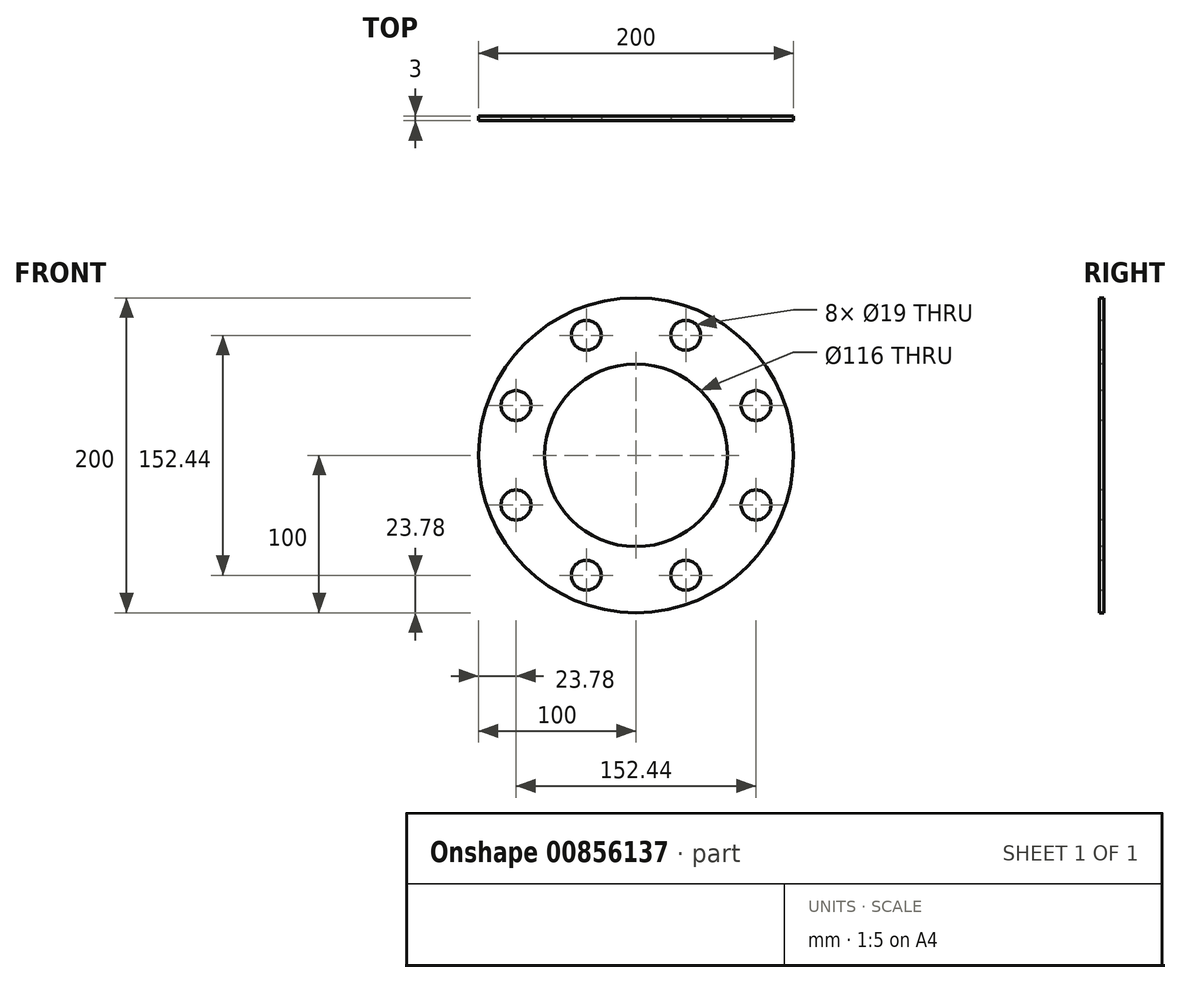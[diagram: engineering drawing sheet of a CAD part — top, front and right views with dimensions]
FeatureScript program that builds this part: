
annotation { "Feature Type Name" : "Feature", "Feature Type Description" : "" }
export const myFeature = defineFeature(function(context is Context, id is Id, definition is map)
    precondition{}
    {
        {
            var Q0;
            Q0=qCreatedBy(makeId("Front.planeOp"),FACE);
            var sketch = newSketch(context, id + "F0", { "sketchPlane" : qUnion([Q0])});
            skCircle(sketch, "E0", {"center": v(0, 0) * mm, "radius": 100 * mm});
            skCircle(sketch, "E1", {"center": v(0, 0) * mm, "radius": 82.5 * mm, "construction": true});
            skLineSegment(sketch, "E2", {"start": v(133.72, 0) * mm, "end": v(-112.74, 0) * mm, "construction": true});
            skLineSegment(sketch, "E3", {"start": v(0, 107.77) * mm, "end": v(0, -109.7) * mm, "construction": true});
            skLineSegment(sketch, "E4", {"start": v(0, 0) * mm, "end": v(85.32, 35.34) * mm, "construction": true});
            skCircle(sketch, "E5", {"center": v(76.22, 31.57) * mm, "radius": 9.5 * mm});
            skCircle(sketch, "E6.1.0", {"center": v(31.57, 76.22) * mm, "radius": 9.5 * mm});
            skCircle(sketch, "E6.2.0", {"center": v(-31.57, 76.22) * mm, "radius": 9.5 * mm});
            skCircle(sketch, "E6.3.0", {"center": v(-76.22, 31.57) * mm, "radius": 9.5 * mm});
            skCircle(sketch, "E6.4.0", {"center": v(-76.22, -31.57) * mm, "radius": 9.5 * mm});
            skCircle(sketch, "E6.5.0", {"center": v(-31.57, -76.22) * mm, "radius": 9.5 * mm});
            skCircle(sketch, "E6.6.0", {"center": v(31.57, -76.22) * mm, "radius": 9.5 * mm});
            skCircle(sketch, "E6.7.0", {"center": v(76.22, -31.57) * mm, "radius": 9.5 * mm});
            skCircle(sketch, "E7", {"center": v(0, 0) * mm, "radius": 58 * mm});
            skSolve(sketch);
        }
        {
            var Q0;
            Q0=makeQuery(id+"F0.imprint","IMPRINT",FACE,{"disambiguationData":[TD([[makeQuery(id+"F0.imprint","IMPRINT",EDGE,{"derivedFrom":sQuery(id+"F0.wireOp",EDGE,"E0")}),1.0]])]});
            extrude(context, id + "F1", {"entities" : qUnion([Q0]), "oppositeDirection" : true, "depth" : 3 * mm, "offsetDistance" : 25 * mm});
        }
    });
